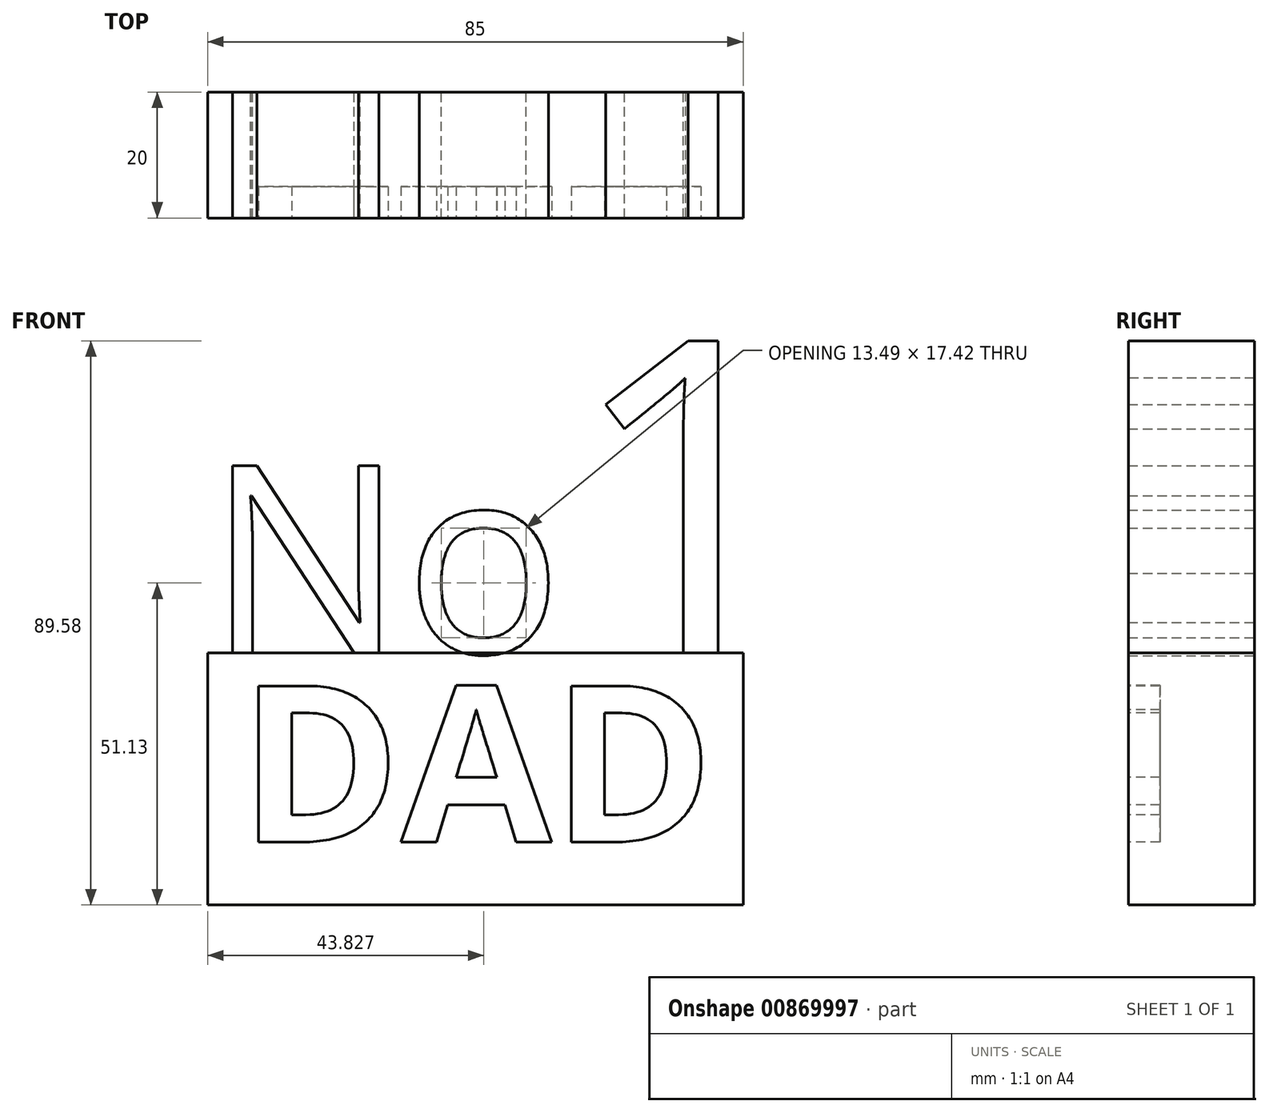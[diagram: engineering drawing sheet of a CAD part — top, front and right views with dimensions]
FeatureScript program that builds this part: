
annotation { "Feature Type Name" : "Feature", "Feature Type Description" : "" }
export const myFeature = defineFeature(function(context is Context, id is Id, definition is map)
    precondition{}
    {
        {
            var Q0;
            Q0=qCreatedBy(makeId("Front.planeOp"),FACE);
            var sketch = newSketch(context, id + "F0", { "sketchPlane" : qUnion([Q0])});
            skText(sketch, "E0", { "text": "No", "fontName": "OpenSans-Regular.ttf"});
            skText(sketch, "E1", { "text": "1", "fontName": "OpenSans-Regular.ttf"});
            const initialGuessF0  = {"E0": [-0.05694, 0, 1, 0, 0.03], "E1": [0, 0, 1, 0, 0.05]};
            skSetInitialGuess(sketch, initialGuessF0);
            skSolve(sketch);
        }
        {
            var Q0;
            Q0 = qSketchRegion(id + "F0", true);
            extrude(context, id + "F1", {"entities" : qUnion([Q0]), "endBound" : BoundingType.SYMMETRIC, "depth" : 20 * mm, "offsetDistance" : 25 * mm});
        }
        {
            var Q0;
            Q0=qCreatedBy(makeId("Front.planeOp"),FACE);
            var sketch = newSketch(context, id + "F2", { "sketchPlane" : qUnion([Q0])});
            skLineSegment(sketch, "E2.bottom", {"start": v(-56.77, 0) * mm, "end": v(28.23, 0) * mm});
            skLineSegment(sketch, "E2.top", {"start": v(-56.77, -40) * mm, "end": v(28.23, -40) * mm});
            skLineSegment(sketch, "E2.left", {"start": v(-56.77, 0) * mm, "end": v(-56.77, -40) * mm});
            skLineSegment(sketch, "E2.right", {"start": v(28.23, 0) * mm, "end": v(28.23, -40) * mm});
            skSolve(sketch);
        }
        {
            var Q0;
            Q0=makeQuery(id+"F2.imprint","IMPRINT",FACE,{"disambiguationData":[TD([[makeQuery(id+"F2.imprint","IMPRINT",EDGE,{"derivedFrom":sQuery(id+"F2.wireOp",EDGE,"E2.bottom")}),-1.0]])]});
            extrude(context, id + "F3", {"entities" : qUnion([Q0]), "endBound" : BoundingType.SYMMETRIC, "depth" : 20 * mm, "offsetDistance" : 25 * mm});
        }
        {
            var Q0;
            Q0=makeQuery(id+"F3.opExtrude","CAP_FACE",FACE,{"disambiguationData":[OSD([sQuery(id+"F2.wireOp",EDGE,"E2.bottom"),sQuery(id+"F2.wireOp",EDGE,"E2.top"),sQuery(id+"F2.wireOp",EDGE,"E2.left"),sQuery(id+"F2.wireOp",EDGE,"E2.right")])],"isStart":false});
            var sketch = newSketch(context, id + "F4", { "sketchPlane" : qUnion([Q0])});
            skText(sketch, "E3", { "text": "DAD", "fontName": "OpenSans-Bold.ttf"});
            const initialGuessF4  = {"E3": [-0.05182, -0.03, 1, 0, 0.025]};
            skSetInitialGuess(sketch, initialGuessF4);
            skSolve(sketch);
        }
        {
            var Q0;
            Q0 = qSketchRegion(id + "F4", true);
            extrude(context, id + "F5", {"entities" : qUnion([Q0]), "operationType" : NewBodyOperationType.REMOVE, "oppositeDirection" : true, "depth" : 5 * mm, "offsetDistance" : 25 * mm});
        }
    });
